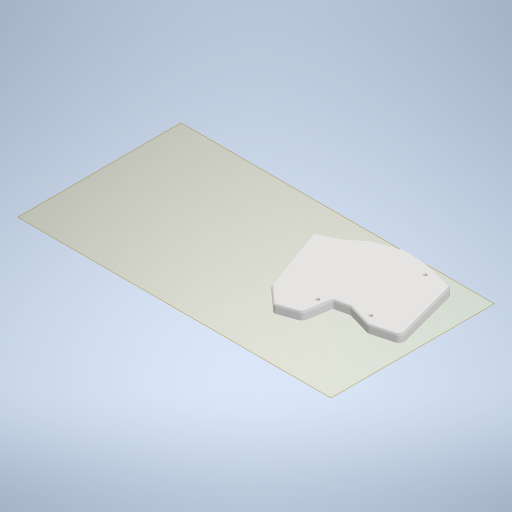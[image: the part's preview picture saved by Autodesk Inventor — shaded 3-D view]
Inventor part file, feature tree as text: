
AUTODESK INVENTOR PART (.ipt)
format: ipt  version: 2024 (Build 280153000, 153)  size: 470,016 bytes
history: native  units: mm
features: reference x11, extrude x5, sketch x5, other x5, plane x2, fillet x1, projected_geometry x1
ambient origin geometry x8: Origin, YZ Plane, XZ Plane, XY Plane, X Axis, Y Axis, Z Axis, Center Point
bodies: Volumenkörper1 (feature_tree)
feature tree (30):
  plane  "Arbeitsebene1"
  extrude  "Extrusion1"  Depth=2.0mm TaperAngle=0.0deg
  extrude  "Extrusion2"  Depth=2.2mm
  fillet  "Rundung1"  Radius=2.2mm
  sketch  "Skizze3"  dims[d7=2.2mm d8=5.0mm]
  plane  "Arbeitsebene2"
  extrude  "Extrusion3"  Depth=5.0mm
  extrude  "Extrusion4"  Depth=5.0mm
  extrude  "Extrusion5"  Depth=10.0mm TaperAngle=0.0deg
  sketch  "Skizze1"  dims[d0=5.0mm d1=0.0mm d2=2.0mm d3=0.0mm]
  reference  "Referenz1"
  reference  "Referenz2"
  reference  "Referenz3"
  reference  "Referenz4"
  reference  "Referenz5"
  sketch  "Skizze2"  dims[d4=2.0mm d5=2.2mm d6=2.2mm]
  projected_geometry  "Projizierte Kontur1"
  reference  "Referenz6"
  reference  "Referenz7"
  reference  "Referenz8"
  sketch  "Skizze4"  dims[d9=5.0mm d10=5.0mm]
  reference  "Referenz9"
  reference  "Referenz10"
  reference  "Referenz11"
  sketch  "Skizze5"  dims[d11=2.0mm d12=0.0mm d13=10.0mm d14=0.0mm d15=3.1mm d16=3.1mm d17=3.1mm d18=2.2mm d19=0.0mm]
  other  "<userpath>\OneDrive\Keyboards\Blavinge\case\case.iam"
  other  "case.iam"
  other  "left_top:1"
  other  "middle_bottom:1"
  other  "blavinge:1"
